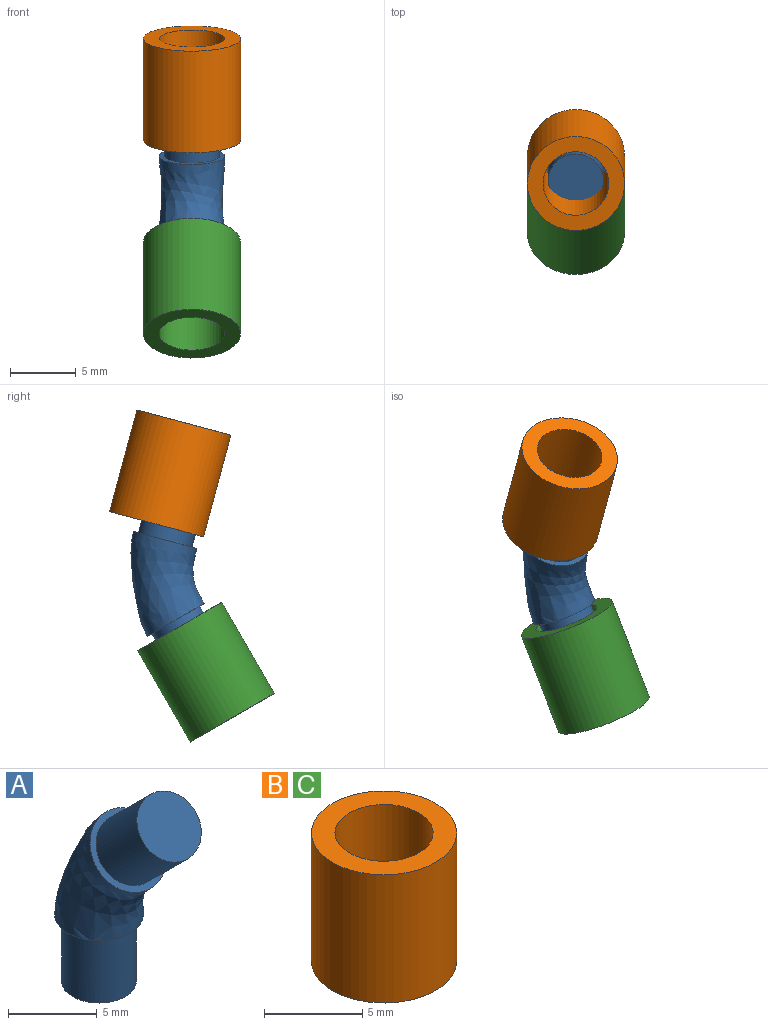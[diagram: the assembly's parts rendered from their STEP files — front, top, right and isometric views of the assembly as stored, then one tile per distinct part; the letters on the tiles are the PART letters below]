
ASSEMBLY  parts=3 mates=1
PART A: 7 faces, bbox 5x9.6x15 mm
  f0: bspline ~5x5mm, area 5.8mm2, adj f2,f4
  f1: bspline ~5x3.53mm, area 5.8mm2, adj f4,f5
  f2: cylinder r=2.1mm len=4.6mm, axis (0,0,1), area 60.7mm2, adj f0,f3
  f3: plane 4.2x4.2mm, normal (0,0,-1), area 13.9mm2, adj f2
  f4: bspline ~7.42x6.61mm, area 94.7mm2, adj f0,f1
  f5: cylinder r=2.1mm len=6.22mm, axis (0,0.71,-0.71), area 60.7mm2, adj f1,f6
  f6: plane 4.2x2.97mm, normal (0,-0.71,0.71), area 13.9mm2, adj f5
PART B: 4 faces, bbox 7.4x7.4x8 mm
  f0: cylinder r=2.5mm len=8mm, axis (0,0,-1), area 125.7mm2, adj f2,f3
  f1: cylinder r=3.7mm len=8mm, axis (0,0,-1), area 186mm2, adj f2,f3
  f2: plane 7.4x7.4mm, normal (0,0,1), area 23.4mm2, adj f0,f1
  f3: plane 7.4x7.4mm, normal (0,0,-1), area 23.4mm2, adj f0,f1
PART C: same geometry as B
PLACE A rot(axis=(-1,0,0),30deg) t=(33.48,47.92,-35.74)mm
PLACE B rot(axis=(1,0,0),15deg) t=(-12.74,23.76,-35.32)mm
PLACE C rot(axis=(-1,0,0),30deg) t=(-12.74,20.65,-29.92)mm
MATE fastened C.f0 <-> A.f2  axis (0,-0.5,-0.87) through (33.48,45.62,-39.72)mm
